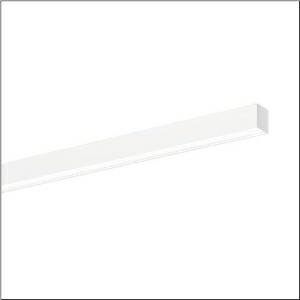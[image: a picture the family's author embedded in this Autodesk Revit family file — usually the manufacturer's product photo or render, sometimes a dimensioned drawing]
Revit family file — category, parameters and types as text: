
# Revit family: silica_r__21_51mx23dc4awb_8ea6
name_source: partatom
category: Lighting Fixtures
units: mm (PartAtom-declared; Revit-internal decimal feet)

## family parameters
Cut with Voids When Loaded = No
Host = Face
Light Source = No
Part Type = Normal
Room Calculation Point = No
Round Connector Dimension = Use Diameter
Shared = No

## types (1)
- --- (1 x LED, 8200 lm, 58.2 W, 4000K)
    Apparent Load = 58 VA
    CIE Flux Codes = 78 96 99 100 100
    Color Rendering = 80
    Color Temperature = 4000K
    Default Elevation = 1800 mm
    Description = Silica® 21, office luminaire, primary optical cover: prismatic diffuser, of PMMA, CAT 2 (L<= 3000cd/m²), light emission: direct distribution, primary light characteristic: symmetric, installation type: surface-mounted, LED, rated luminous flux: 8.200lm, luminous efficacy: 141lm/W, light colour: 840, colour temperature: 4000K, control gear: DALI 2, with terminal, 3+2-pole, max. 2.5mm², mains connection: 220..240V, AC, 50/60Hz, rated input power: 58.2W, luminaire housing, of aluminium, traffic white (RAL 9016), length: 3.004mm, width: 53mm, height: 53mm, protection rating (complete): IP20, insulation class (complete): insulation class I (protective earthing), certification: CE, permissible operating ambient temperature: 0..+35°C, standard: EN 50419, packaging unit: 1 piece
    Height = 53 mm
    Lamp = 1 x LED
    Lamp Light Flux = 8200 lm
    Lamp Power = 58.2 W
    Lamp count = 1
    Length = 3004 mm
    Luminous efficacy = 141 lm/W
    Manufacturer = Siteco
    ModVariant = No
    Model = 51MX23DC4AWB
    Mounting Place = Ceiling
    Mounting Type = Surface mounted
    Number of Poles = 1
    OnlyDefault = Yes
    Power Factor = 1
    Product Name = Silica® 21
    Product group = office luminaire | ceiling mounted
    ProductGroupID = 302
    Protection Class = Protection class I
    Protection Degree = IP 20
    RLX_Detail_Level = 1
    RLX_Emergency_Light_Flux = 0 lm
    RLX_Emergency_Type = 0
    RLX_Emergency_Type_DB = No
    RlxData = <blob elided: 18721 chars, md5=93141965>
    Socket = socket
    Standby Power = 0 W
    System Light Flux = 8200 lm
    System Power = 58 W
    Type Comments = factory setting: luminous flux: 100 % | dim-lin: 254 | 323 mA
    Type Image = l_1335877.jpg
    URL = http://relux.com
    VarID = @adj_119506
    Voltage = 0 V
    Weight = 0.00 kg
    Width = 53 mm

## geometry (parser evidence)
native form markers: Blend x4, Sweep x11
no freeform markers — native parametric forms only
